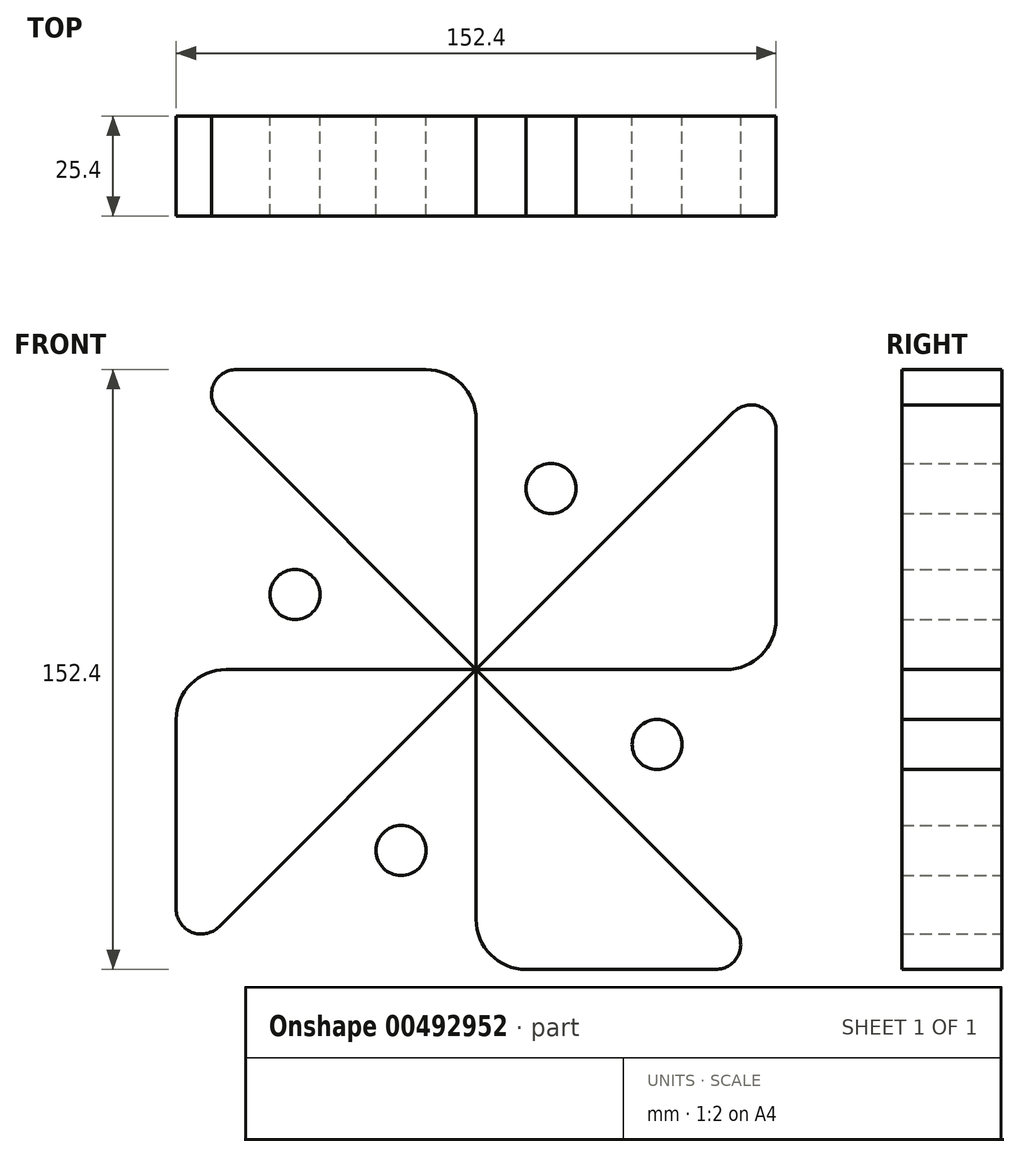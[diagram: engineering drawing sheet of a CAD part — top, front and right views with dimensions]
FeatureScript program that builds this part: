
annotation { "Feature Type Name" : "Feature", "Feature Type Description" : "" }
export const myFeature = defineFeature(function(context is Context, id is Id, definition is map)
    precondition{}
    {
        {
            var Q0;
            Q0=qCreatedBy(makeId("Front.planeOp"),FACE);
            var sketch = newSketch(context, id + "F0", { "sketchPlane" : qUnion([Q0])});
            skLineSegment(sketch, "E0", {"start": v(0, 0) * mm, "end": v(63.5, 0) * mm});
            skLineSegment(sketch, "E1", {"start": v(76.2, 12.7) * mm, "end": v(76.2, 60.87) * mm});
            skLineSegment(sketch, "E2", {"start": v(65.36, 65.36) * mm, "end": v(0, 0) * mm});
            skLineSegment(sketch, "E3", {"start": v(0, 0) * mm, "end": v(0, 63.5) * mm});
            skLineSegment(sketch, "E4", {"start": v(-12.7, 76.2) * mm, "end": v(-60.87, 76.2) * mm});
            skLineSegment(sketch, "E5", {"start": v(-65.36, 65.36) * mm, "end": v(0, 0) * mm});
            skLineSegment(sketch, "E6", {"start": v(0, 0) * mm, "end": v(-63.5, 0) * mm});
            skLineSegment(sketch, "E7", {"start": v(-76.2, -12.7) * mm, "end": v(-76.2, -60.87) * mm});
            skLineSegment(sketch, "E8", {"start": v(-65.36, -65.36) * mm, "end": v(0, 0) * mm});
            skLineSegment(sketch, "E9", {"start": v(0, 0) * mm, "end": v(0, -63.5) * mm});
            skLineSegment(sketch, "E10", {"start": v(12.7, -76.2) * mm, "end": v(60.87, -76.2) * mm});
            skLineSegment(sketch, "E11", {"start": v(65.36, -65.36) * mm, "end": v(0, 0) * mm});
            skPoint(sketch, "E12.visualSharp", {"position": v(-76.2, 0) * mm});
            skArc(sketch, "E12.filletArc", {"start": v(-63.5, 0) * mm, "mid": v(-72.48, -3.72) * mm, "end": v(-76.2, -12.7) * mm});
            skPoint(sketch, "E13.visualSharp", {"position": v(0, -76.2) * mm});
            skArc(sketch, "E13.filletArc", {"start": v(0, -63.5) * mm, "mid": v(3.72, -72.48) * mm, "end": v(12.7, -76.2) * mm});
            skPoint(sketch, "E14.visualSharp", {"position": v(76.2, 0) * mm});
            skArc(sketch, "E14.filletArc", {"start": v(63.5, 0) * mm, "mid": v(72.48, 3.72) * mm, "end": v(76.2, 12.7) * mm});
            skPoint(sketch, "E15.visualSharp", {"position": v(0, 76.2) * mm});
            skArc(sketch, "E15.filletArc", {"start": v(0, 63.5) * mm, "mid": v(-3.72, 72.48) * mm, "end": v(-12.7, 76.2) * mm});
            skPoint(sketch, "E16.visualSharp", {"position": v(-76.2, 76.2) * mm});
            skArc(sketch, "E16.filletArc", {"start": v(-60.87, 76.2) * mm, "mid": v(-66.74, 72.28) * mm, "end": v(-65.36, 65.36) * mm});
            skPoint(sketch, "E17.visualSharp", {"position": v(-76.2, -76.2) * mm});
            skArc(sketch, "E17.filletArc", {"start": v(-76.2, -60.87) * mm, "mid": v(-72.28, -66.74) * mm, "end": v(-65.36, -65.36) * mm});
            skPoint(sketch, "E18.visualSharp", {"position": v(76.2, -76.2) * mm});
            skArc(sketch, "E18.filletArc", {"start": v(60.87, -76.2) * mm, "mid": v(66.74, -72.28) * mm, "end": v(65.36, -65.36) * mm});
            skPoint(sketch, "E19.visualSharp", {"position": v(76.2, 76.2) * mm});
            skArc(sketch, "E19.filletArc", {"start": v(76.2, 60.87) * mm, "mid": v(72.28, 66.74) * mm, "end": v(65.36, 65.36) * mm});
            skCircle(sketch, "E20", {"center": v(-46, 19.05) * mm, "radius": 6.35 * mm});
            skCircle(sketch, "E21", {"center": v(19.05, 46) * mm, "radius": 6.35 * mm});
            skCircle(sketch, "E22", {"center": v(46, -19.05) * mm, "radius": 6.35 * mm});
            skCircle(sketch, "E23", {"center": v(-19.05, -46) * mm, "radius": 6.35 * mm});
            skSolve(sketch);
        }
        {
            var Q0;
            Q0 = qSketchRegion(id + "F0", true);
            extrude(context, id + "F1", {"entities" : qUnion([Q0]), "depth" : 25.4 * mm, "offsetDistance" : 25.4 * mm});
        }
        {
            var Q0;
            Q0=qCreatedBy(makeId("Front.planeOp"),FACE);
            var sketch = newSketch(context, id + "F2", { "sketchPlane" : qUnion([Q0])});
            skCircle(sketch, "E24", {"center": v(0, 0) * mm, "radius": 6.35 * mm});
            skSolve(sketch);
        }
        {
            var Q0;
            Q0=sQuery(id+"F2.wireOp",EDGE,"E24");
            extrude(context, id + "F3", {"bodyType" : ToolBodyType.SURFACE, "surfaceEntities" : qUnion([Q0]), "depth" : 254 * mm, "offsetDistance" : 25.4 * mm});
        }
    });
